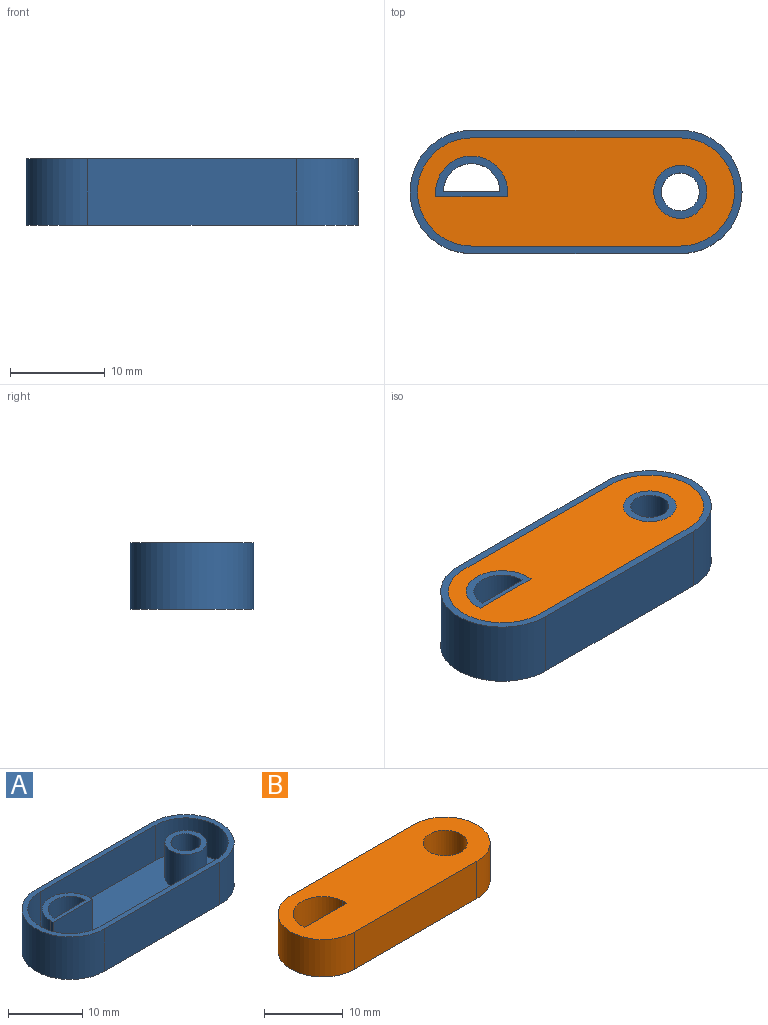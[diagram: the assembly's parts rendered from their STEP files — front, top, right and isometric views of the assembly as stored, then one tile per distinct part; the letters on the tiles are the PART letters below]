
ASSEMBLY  parts=2 mates=1
PART A: 21 faces, bbox 35x13x7 mm
  f0: plane 7.57x5.8mm, normal (0,-1,0), area 43.9mm2, adj f1,f5,f6,f20
  f1: plane 5.8x0.8mm, normal (1,0,0), area 4.6mm2, adj f0,f2,f6,f20
  f2: cylinder r=3.79mm len=7.57mm, axis (0,0,-1), area 67.4mm2, adj f1,f5,f6,f20
  f3: plane 7x5.98mm, normal (0,1,0), area 41.8mm2, adj f4,f6,f7
  f4: cylinder r=2.99mm len=7mm, axis (0,0,-1), area 65.7mm2, adj f3,f6,f7
  f5: plane 5.8x0.53mm, normal (-1,0,0), area 3.1mm2, adj f0,f2,f6,f20
  f6: plane 7.57x4.32mm, normal (0,0,1), area 12.5mm2, adj f0,f1,f2,f3,f4,f5
  f7: plane 35x13mm, normal (0,0,-1), area 392.1mm2, adj f3,f4,f8,f11,f12,f13,f18
  f8: cylinder r=2mm len=7mm, axis (0,0,-1), area 88mm2, adj f7,f10
  f9: cylinder r=2.8mm len=5.8mm, axis (0,0,-1), area 102mm2, adj f10,f20
  f10: plane 5.6x5.6mm, normal (0,0,1), area 12.1mm2, adj f8,f9
  f11: plane 22x7mm, normal (0,-1,0), area 154mm2, adj f7,f12,f18,f19
  f12: cylinder r=6.5mm len=13mm, axis (0,0,-1), area 142.9mm2, adj f7,f11,f13,f19
  f13: plane 22x7mm, normal (0,1,0), area 154mm2, adj f7,f12,f18,f19
  f14: cylinder r=5.7mm len=11.4mm, axis (0,0,-1), area 103.9mm2, adj f15,f17,f19,f20
  f15: plane 22x5.8mm, normal (0,1,0), area 127.6mm2, adj f14,f16,f19,f20
  f16: cylinder r=5.7mm len=11.4mm, axis (0,0,-1), area 103.9mm2, adj f15,f17,f19,f20
  f17: plane 22x5.8mm, normal (0,-1,0), area 127.6mm2, adj f14,f16,f19,f20
  f18: cylinder r=6.5mm len=13mm, axis (0,0,-1), area 142.9mm2, adj f7,f11,f13,f19
  f19: plane 35x13mm, normal (0,0,1), area 65.9mm2, adj f11,f12,f13,f14,f15,f16,f17,f18
  f20: plane 33.4x11.4mm, normal (0,0,1), area 301.7mm2, adj f0,f1,f2,f5,f9,f14,f15,f16
PART B: 11 faces, bbox 33.4x11.4x5.8 mm
  f0: plane 22x5.8mm, normal (0,-1,0), area 127.6mm2, adj f1,f8,f9,f10
  f1: cylinder r=5.7mm len=11.4mm, axis (0,0,-1), area 103.9mm2, adj f0,f2,f9,f10
  f2: plane 22x5.8mm, normal (0,1,0), area 127.6mm2, adj f1,f8,f9,f10
  f3: plane 7.57x5.8mm, normal (0,1,0), area 43.9mm2, adj f4,f6,f9,f10
  f4: plane 5.8x0.53mm, normal (1,0,0), area 3.1mm2, adj f3,f5,f9,f10
  f5: cylinder r=3.79mm len=7.57mm, axis (0,0,-1), area 67.4mm2, adj f4,f6,f9,f10
  f6: plane 5.8x0.8mm, normal (-1,0,0), area 4.6mm2, adj f3,f5,f9,f10
  f7: cylinder r=2.8mm len=5.8mm, axis (0,0,-1), area 102mm2, adj f9,f10
  f8: cylinder r=5.7mm len=11.4mm, axis (0,0,-1), area 103.9mm2, adj f0,f2,f9,f10
  f9: plane 33.4x11.4mm, normal (0,0,1), area 301.7mm2, adj f0,f1,f2,f3,f4,f5,f6,f7
  f10: plane 33.4x11.4mm, normal (0,0,-1), area 301.7mm2, adj f0,f1,f2,f3,f4,f5,f6,f7
PLACE A t=(-3.75,-0.99,-3.1)mm fixed
PLACE B t=(-5.85,-0.86,-1.9)mm
MATE fastened A.f20 <-> B.f10  axis (0,0,1) through (-2.11,-1.11,-1.9)mm
